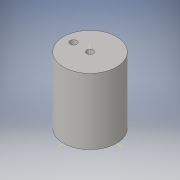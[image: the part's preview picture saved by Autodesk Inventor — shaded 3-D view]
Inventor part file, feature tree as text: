
AUTODESK INVENTOR PART (.ipt)
format: ipt  version: 2016 (Build 200138000, 138)  size: 120,320 bytes
history: native  units: mm
features: extrude x6, sketch x6
ambient origin geometry x8: Origin, YZ Plane, XZ Plane, XY Plane, X Axis, Y Axis, Z Axis, Center Point
bodies: Volumenkörper1 (feature_tree)
feature tree (12):
  extrude  "Extrusion1"  Depth=10.0mm TaperAngle=0.0deg
  extrude  "Extrusion2"  Depth=9.0mm TaperAngle=0.0deg
  extrude  "Extrusion3"  Depth=1.0mm
  extrude  "Extrusion4"  Depth=1.0mm
  extrude  "Extrusion5"  TaperAngle=0.0deg  [1 undecoded]
  extrude  "Extrusion6"  Depth=1.0mm
  sketch  "Skizze1"  dims[d0=8.0mm d1=10.0mm d2=0.0mm]
  sketch  "Skizze2"  dims[d3=7.0mm d4=9.0mm d5=0.0mm]
  sketch  "Skizze3"  dims[d6=1.0mm d7=0.0mm d8=1.0mm]
  sketch  "Skizze4"  dims[d9=1.0mm d10=0.0mm d11=1.0mm]
  sketch  "Skizze5"  dims[d12=2.5mm d13=0.0mm]
  sketch  "Skizze6"  dims[d14=1.0mm d15=0.0mm d16=1.0mm d17=2.5mm d18=0.0mm d19=1.0mm d20=0.0mm]
note: 1 required parameter value undecoded (feature->parameter linkage not recoverable at this tier; creation-order binding heuristic only, values carry confidence <= 0.55)
